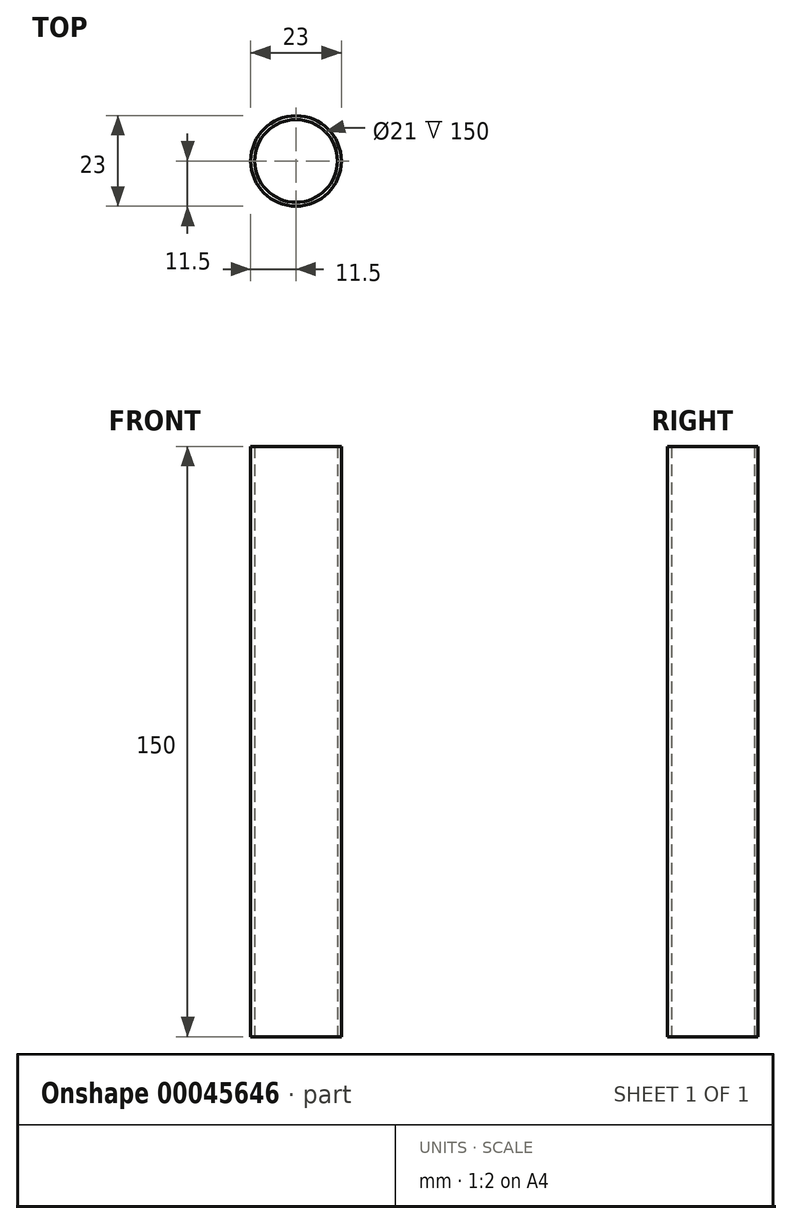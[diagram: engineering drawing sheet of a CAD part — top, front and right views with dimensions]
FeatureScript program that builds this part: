
annotation { "Feature Type Name" : "Feature", "Feature Type Description" : "" }
export const myFeature = defineFeature(function(context is Context, id is Id, definition is map)
    precondition{}
    {
        {
            var Q0;
            Q0=qCreatedBy(makeId("Top.planeOp"),FACE);
            var sketch = newSketch(context, id + "F0", { "sketchPlane" : qUnion([Q0])});
            skCircle(sketch, "E0", {"center": v(0, 0) * mm, "radius": 11.5 * mm});
            skCircle(sketch, "E1", {"center": v(0, 0) * mm, "radius": 10.5 * mm});
            skSolve(sketch);
        }
        {
            var Q0;
            Q0=makeQuery(id+"F0.imprint","IMPRINT",FACE,{"disambiguationData":[TD([[makeQuery(id+"F0.imprint","IMPRINT",EDGE,{"derivedFrom":sQuery(id+"F0.wireOp",EDGE,"E0")}),1.0]])]});
            extrude(context, id + "F1", {"entities" : qUnion([Q0]), "depth" : 150 * mm});
        }
    });
